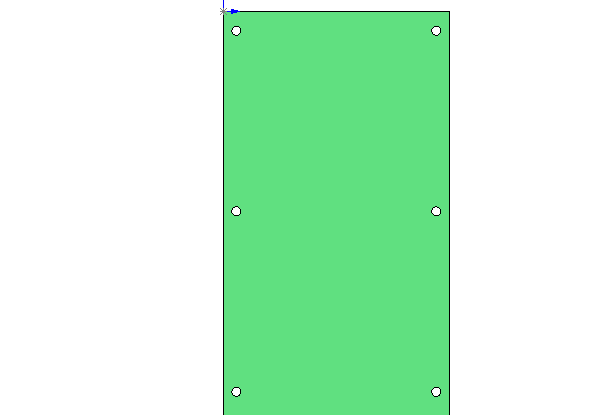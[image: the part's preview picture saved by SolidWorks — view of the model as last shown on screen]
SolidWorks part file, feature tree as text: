
SOLIDWORKS PART (.sldprt)
format: sldprt  version: not decoded by parser v0  size: 137,216 bytes
history: native  units: mm
features: sketch x2, material x1, extrude x1, cut_extrude x1, pattern_linear x1 (+13 scaffold rows collapsed)
feature tree (19):
  scaffold x13  (default folders/planes/origin — collapsed)
  material  "Material <not specified>"
  sketch  "Sketch1"  dims[D1=88.9mm D2=228.6mm]
  extrude  "Extrude1"  Depth=1.5748mm
  sketch  "Sketch2"  dims[c1.D1=~5.013902mm c1.D2=3.556mm c2.D1=7.62mm c2.D3=5.08mm]
  cut_extrude  "Cut-Extrude1"  Depth=2.54mm
  pattern_linear  "LPattern1"  Count1=2 Count2=4 Spacing1=78.74mm Spacing2=71.12mm
decode coverage: 5 of 5 modeling features carry decoded parameters
note: ~ marks probable driven/reference dimensions
note: suppression state not decoded; provenance and decode notes live in map.json
